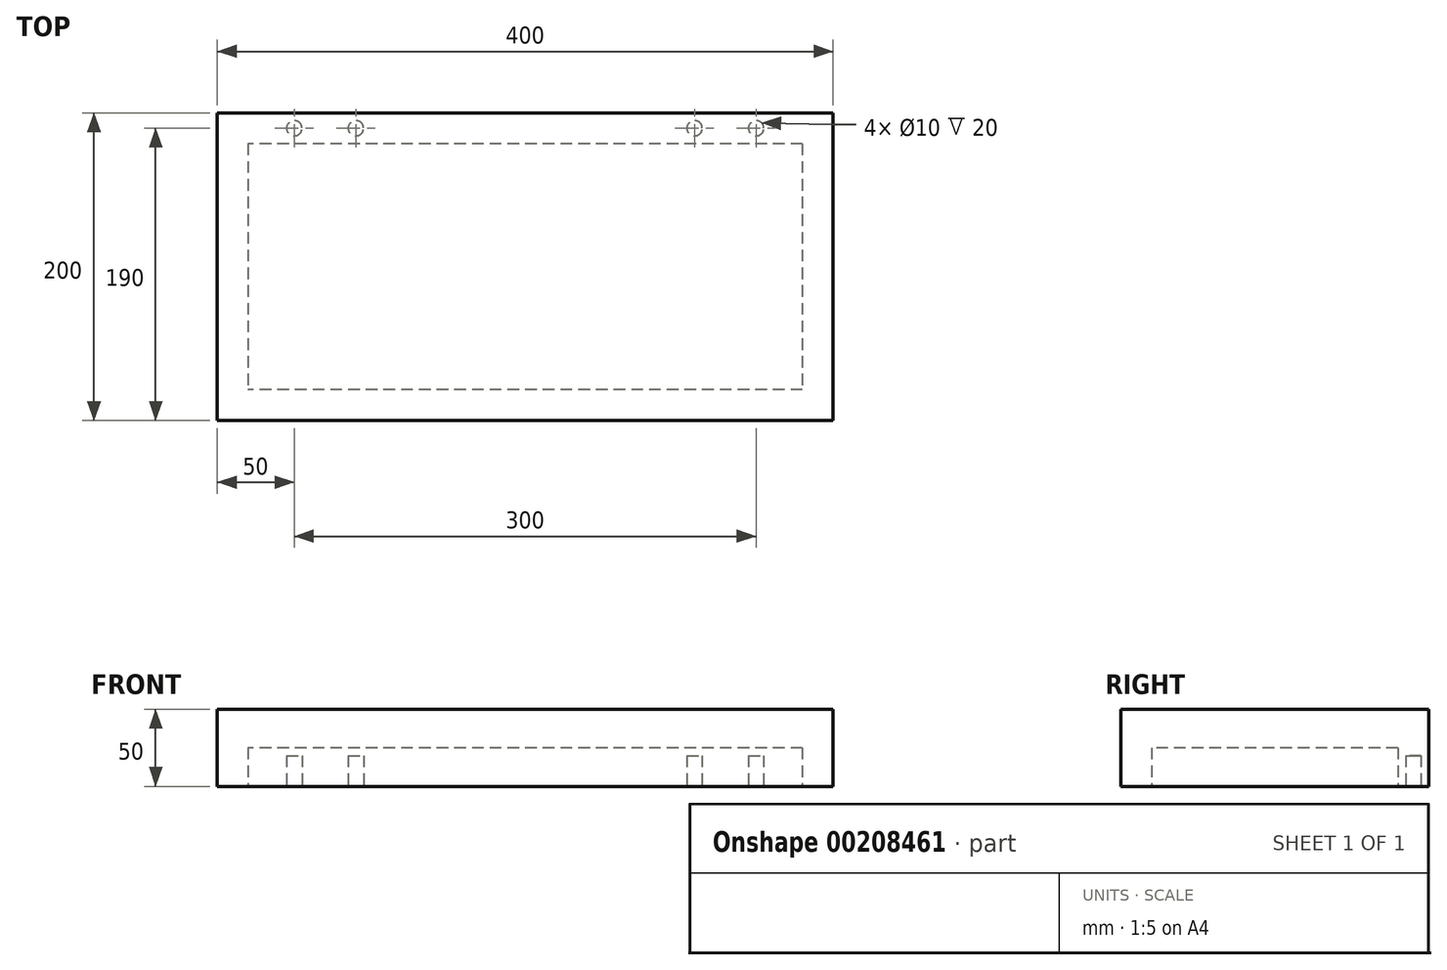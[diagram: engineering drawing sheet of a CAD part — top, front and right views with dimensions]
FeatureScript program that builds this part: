
annotation { "Feature Type Name" : "Feature", "Feature Type Description" : "" }
export const myFeature = defineFeature(function(context is Context, id is Id, definition is map)
    precondition{}
    {
        {
            var Q0;
            Q0=qCreatedBy(makeId("Top.planeOp"),FACE);
            var sketch = newSketch(context, id + "F0", { "sketchPlane" : qUnion([Q0])});
            skLineSegment(sketch, "E0.bottom", {"start": v(200, -100) * mm, "end": v(-200, -100) * mm});
            skLineSegment(sketch, "E0.top", {"start": v(200, 100) * mm, "end": v(-200, 100) * mm});
            skLineSegment(sketch, "E0.left", {"start": v(200, -100) * mm, "end": v(200, 100) * mm});
            skLineSegment(sketch, "E0.right", {"start": v(-200, -100) * mm, "end": v(-200, 100) * mm});
            skPoint(sketch, "E0.middle", {"position": v(0, 0) * mm});
            skSolve(sketch);
        }
        {
            var Q0;
            Q0=qSketchRegion(id+"F0",true);
            extrude(context, id + "F1", {"entities" : qUnion([Q0]), "depth" : 50 * mm});
        }
        {
            var Q0;
            Q0=makeQuery(id+"F1.opExtrude","CAP_FACE",FACE,{"disambiguationData":[OSD([sQuery(id+"F0.wireOp",EDGE,"E0.bottom"),sQuery(id+"F0.wireOp",EDGE,"E0.top"),sQuery(id+"F0.wireOp",EDGE,"E0.left"),sQuery(id+"F0.wireOp",EDGE,"E0.right")])],"isStart":true});
            var sketch = newSketch(context, id + "F2", { "sketchPlane" : qUnion([Q0])});
            skLineSegment(sketch, "E1.bottom", {"start": v(180, -80) * mm, "end": v(-180, -80) * mm});
            skLineSegment(sketch, "E1.top", {"start": v(180, 80) * mm, "end": v(-180, 80) * mm});
            skLineSegment(sketch, "E1.left", {"start": v(180, -80) * mm, "end": v(180, 80) * mm});
            skLineSegment(sketch, "E1.right", {"start": v(-180, -80) * mm, "end": v(-180, 80) * mm});
            skPoint(sketch, "E1.middle", {"position": v(0, 0) * mm});
            skSolve(sketch);
        }
        {
            var Q0;
            Q0=qSketchRegion(id+"F2",true);
            extrude(context, id + "F3", {"entities" : qUnion([Q0]), "operationType" : NewBodyOperationType.REMOVE, "oppositeDirection" : true, "depth" : 25 * mm});
        }
        {
            var Q0;
            Q0=makeQuery(id+"F1.opExtrude","CAP_FACE",FACE,{"disambiguationData":[OSD([sQuery(id+"F0.wireOp",EDGE,"E0.bottom"),sQuery(id+"F0.wireOp",EDGE,"E0.top"),sQuery(id+"F0.wireOp",EDGE,"E0.left"),sQuery(id+"F0.wireOp",EDGE,"E0.right")])],"isStart":true});
            var sketch = newSketch(context, id + "F4", { "sketchPlane" : qUnion([Q0])});
            skCircle(sketch, "E2", {"center": v(-150, -90) * mm, "radius": 5 * mm});
            skCircle(sketch, "E3", {"center": v(-110, -90) * mm, "radius": 5 * mm});
            skLineSegment(sketch, "E4", {"start": v(0, -80) * mm, "end": v(0, -100) * mm, "construction": true});
            skCircle(sketch, "E5.MirrorC", {"center": v(110, -90) * mm, "radius": 5 * mm});
            skCircle(sketch, "E6.MirrorC", {"center": v(150, -90) * mm, "radius": 5 * mm});
            skSolve(sketch);
        }
        {
            var Q0;
            Q0=qSketchRegion(id+"F4",true);
            extrude(context, id + "F5", {"entities" : qUnion([Q0]), "operationType" : NewBodyOperationType.REMOVE, "oppositeDirection" : true, "depth" : 20 * mm});
        }
    });
